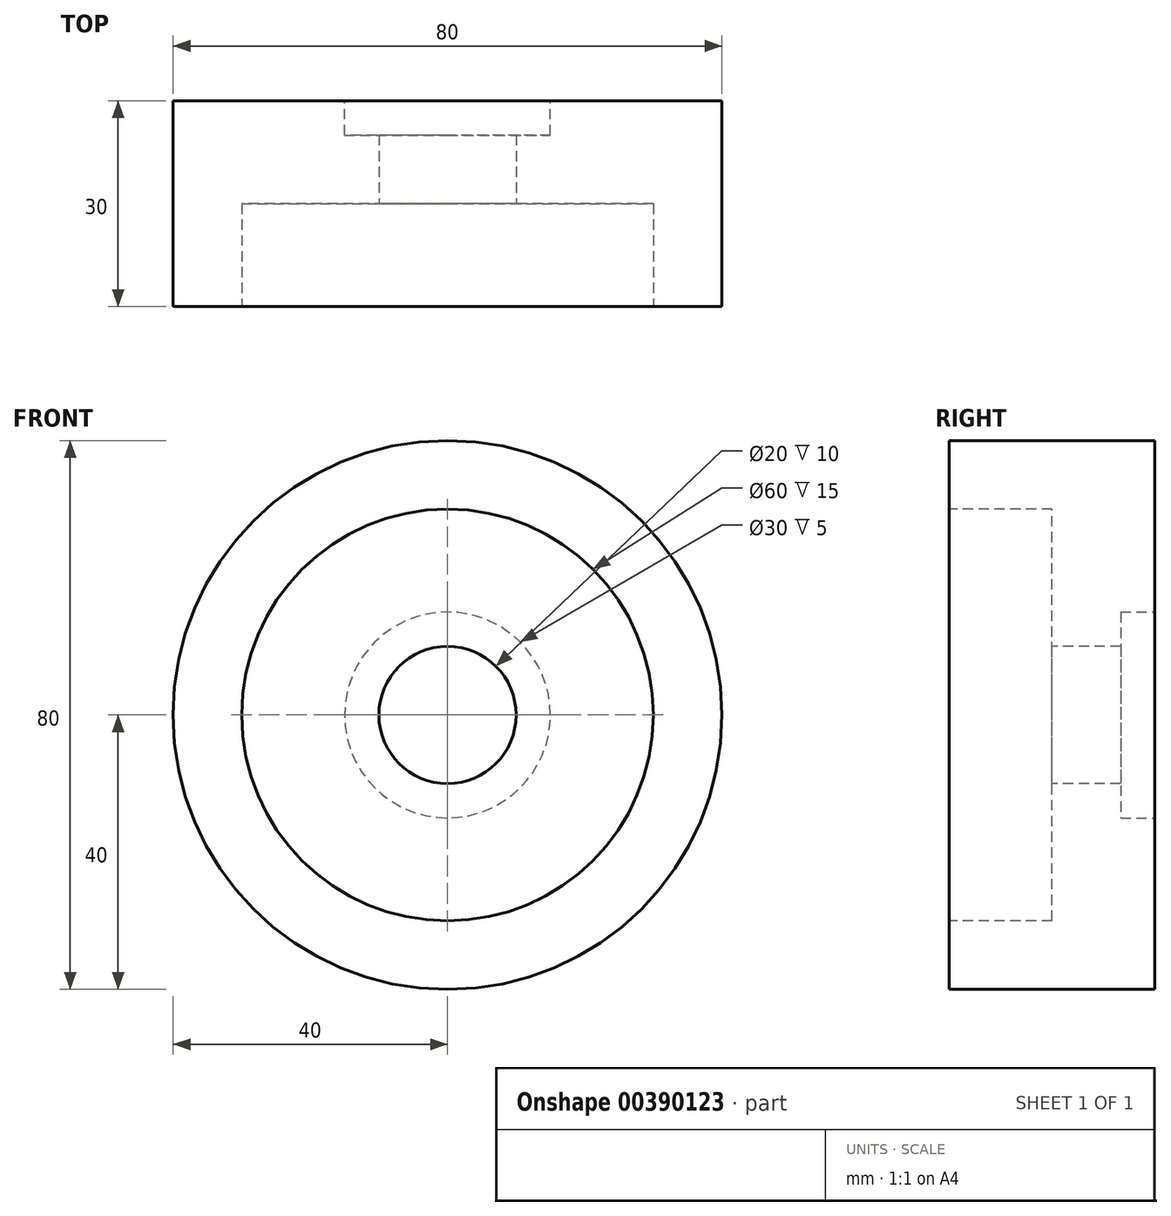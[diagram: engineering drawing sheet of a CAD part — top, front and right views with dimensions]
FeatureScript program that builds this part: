
annotation { "Feature Type Name" : "Feature", "Feature Type Description" : "" }
export const myFeature = defineFeature(function(context is Context, id is Id, definition is map)
    precondition{}
    {
        {
            var Q0;
            Q0=qCreatedBy(makeId("Front.planeOp"),FACE);
            var sketch = newSketch(context, id + "F0", { "sketchPlane" : qUnion([Q0])});
            skCircle(sketch, "E0", {"center": v(0, 0) * mm, "radius": 40 * mm});
            skSolve(sketch);
        }
        {
            var Q0;
            Q0=makeQuery(id+"F0.imprint","IMPRINT",FACE,{"disambiguationData":[TD([[makeQuery(id+"F0.imprint","IMPRINT",EDGE,{"derivedFrom":sQuery(id+"F0.wireOp",EDGE,"E0")}),1.0]])]});
            extrude(context, id + "F1", {"entities" : qUnion([Q0]), "oppositeDirection" : true, "depth" : 30 * mm});
        }
        {
            var Q0;
            Q0=sQuery(id+"F0.wireOp",VERTEX,"E0.center");
            var Q1;
            Q1=makeQuery(id+"F1.opExtrude","SWEPT_BODY",BODY,{"disambiguationData":[OSD([sQuery(id+"F0.wireOp",EDGE,"E0")])]});
            hole(context, id + "F2", {"style" : HoleStyle.C_BORE, "endStyle" : HoleEndStyle.THROUGH, "holeDiameter" : 20 * mm, "cBoreDiameter" : 60 * mm, "cBoreDepth" : 15 * mm, "isTappedThrough" : true, "tappedDepth" : 12 * mm, "tapClearance" : 3, "startFromSketch" : true, "locations" : qUnion([Q0]), "scope" : qUnion([Q1]), "majorDiameter" : 5 * mm});
        }
        {
            var Q0;
            Q0=makeQuery(id+"F1.opExtrude","CAP_FACE",FACE,{"disambiguationData":[OSD([sQuery(id+"F0.wireOp",EDGE,"E0")])],"isStart":false});
            var sketch = newSketch(context, id + "F3", { "sketchPlane" : qUnion([Q0])});
            skCircle(sketch, "E1", {"center": v(0, 0) * mm, "radius": 15 * mm});
            skSolve(sketch);
        }
        {
            var Q0;
            Q0=sQuery(id+"F3.wireOp",VERTEX,"E1.center");
            var Q1;
            Q1=makeQuery(id+"F1.opExtrude","SWEPT_BODY",BODY,{"disambiguationData":[OSD([sQuery(id+"F0.wireOp",EDGE,"E0")])]});
            hole(context, id + "F4", {"style" : HoleStyle.C_BORE, "endStyle" : HoleEndStyle.BLIND, "holeDiameter" : 20 * mm, "cBoreDiameter" : 30 * mm, "cBoreDepth" : 5 * mm, "holeDepth" : 50 * mm, "isTappedThrough" : true, "tappedDepth" : 12 * mm, "tapClearance" : 3, "locations" : qUnion([Q0]), "scope" : qUnion([Q1])});
        }
    });
